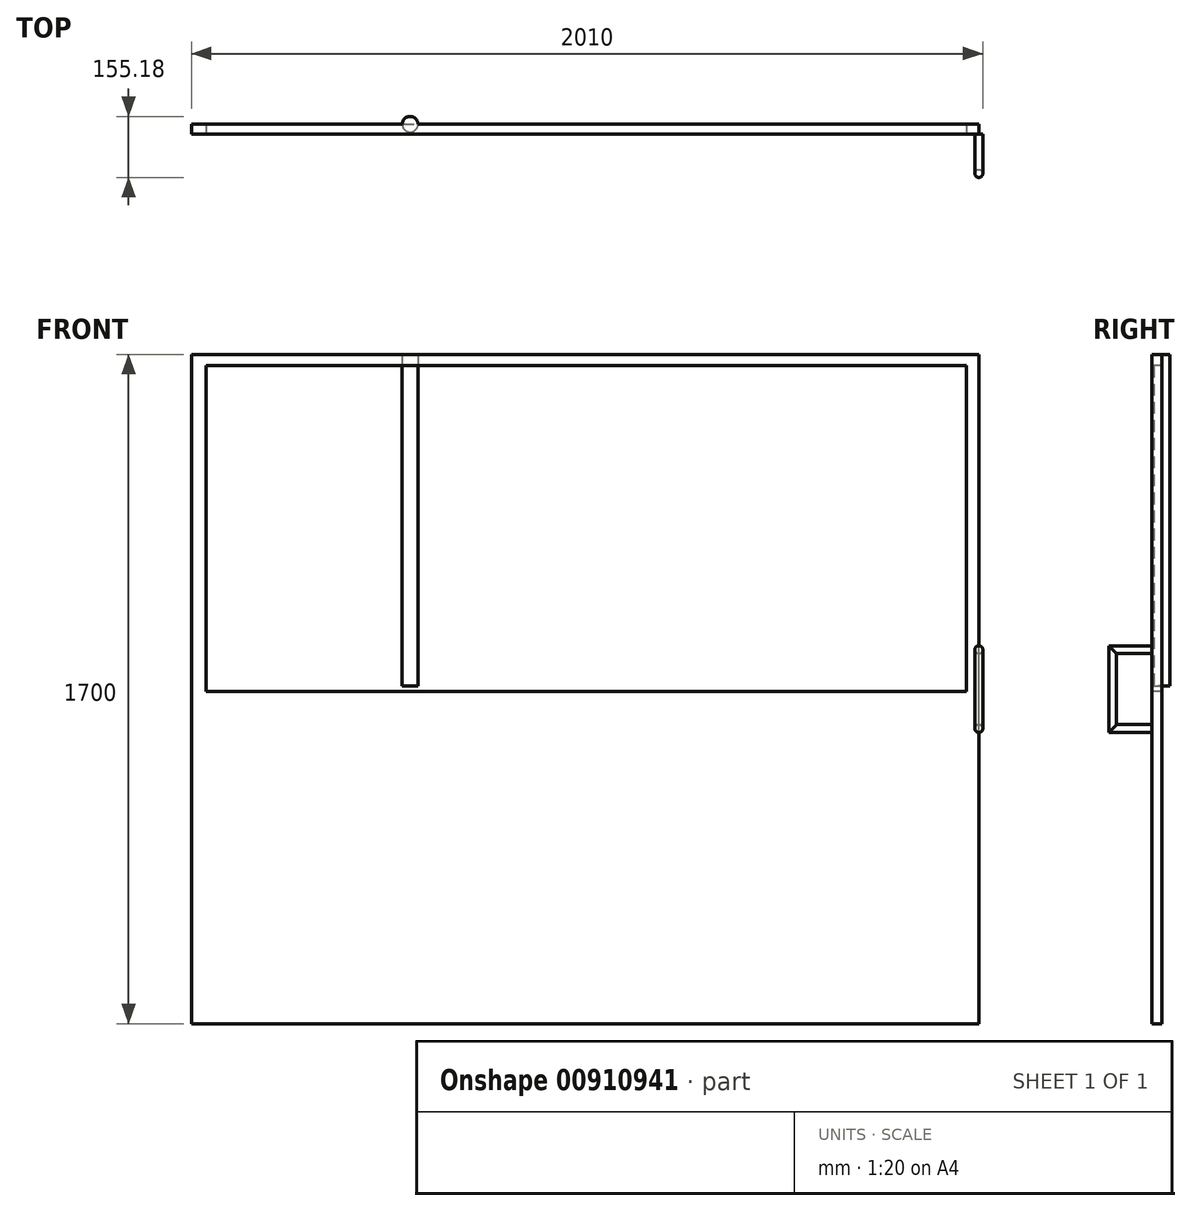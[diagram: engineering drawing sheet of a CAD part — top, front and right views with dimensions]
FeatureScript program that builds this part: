
annotation { "Feature Type Name" : "Feature", "Feature Type Description" : "" }
export const myFeature = defineFeature(function(context is Context, id is Id, definition is map)
    precondition{}
    {
        {
            var Q0;
            Q0=qCreatedBy(makeId("Front.planeOp"),FACE);
            var sketch = newSketch(context, id + "F0", { "sketchPlane" : qUnion([Q0])});
            skLineSegment(sketch, "E0.bottom", {"start": v(0, 0) * mm, "end": v(1000, 0) * mm});
            skLineSegment(sketch, "E0.top", {"start": v(0, 1700) * mm, "end": v(1000, 1700) * mm});
            skLineSegment(sketch, "E0.right", {"start": v(1000, 0) * mm, "end": v(1000, 1700) * mm});
            skLineSegment(sketch, "E1.MirrorCS", {"start": v(0, 1700) * mm, "end": v(-1000, 1700) * mm});
            skLineSegment(sketch, "E2.MirrorCS", {"start": v(-1000, 0) * mm, "end": v(-1000, 1700) * mm});
            skLineSegment(sketch, "E3.MirrorCS", {"start": v(0, 0) * mm, "end": v(-1000, 0) * mm});
            skSolve(sketch);
        }
        {
            var Q0;
            Q0 = qSketchRegion(id + "F0", true);
            extrude(context, id + "F1", {"entities" : qUnion([Q0]), "depth" : 25 * mm, "offsetDistance" : 25 * mm});
        }
        {
            var Q0;
            Q0=makeQuery(id+"F1.opExtrude","SWEPT_FACE",FACE,{"disambiguationData":[OSD([sQuery(id+"F0.wireOp",EDGE,"E0.right")])]});
            var sketch = newSketch(context, id + "F2", { "sketchPlane" : qUnion([Q0])});
            skPoint(sketch, "E4.start.orphan", {"position": v(-25, 850) * mm});
            skLineSegment(sketch, "E5", {"start": v(-25, 950) * mm, "end": v(-125, 950) * mm});
            skLineSegment(sketch, "E6", {"start": v(-125, 950) * mm, "end": v(-125, 750) * mm});
            skLineSegment(sketch, "E7", {"start": v(-125, 750) * mm, "end": v(-25, 750) * mm});
            skSolve(sketch);
        }
        {
            var Q0;
            Q0=makeQuery(id+"F1.opExtrude","CAP_FACE",FACE,{"disambiguationData":[OSD([sQuery(id+"F0.wireOp",EDGE,"E0.bottom"),sQuery(id+"F0.wireOp",EDGE,"E0.top"),sQuery(id+"F0.wireOp",EDGE,"E0.right"),sQuery(id+"F0.wireOp",EDGE,"E1.MirrorCS"),sQuery(id+"F0.wireOp",EDGE,"E2.MirrorCS"),sQuery(id+"F0.wireOp",EDGE,"E3.MirrorCS")])],"isStart":false});
            var sketch = newSketch(context, id + "F3", { "sketchPlane" : qUnion([Q0])});
            skCircle(sketch, "E8", {"center": v(1000, 950.18) * mm, "radius": 10 * mm});
            skSolve(sketch);
        }
        {
            var Q0;
            {var subQ0=sQuery(id+"F3.wireOp",EDGE,"E8");var subQ1=makeQuery(id+"F1.opExtrude","CAP_EDGE",EDGE,{"disambiguationData":[OSD([sQuery(id+"F0.wireOp",EDGE,"E0.right")])],"isStart":false});var subQ2=makeQuery(id+"F3.imprint","INTERSECT",VERTEX,{"disambiguationData":[OD(0.0)],"derivedFrom":[subQ1,subQ0]});Q0=makeQuery(id+"F3.imprint","IMPRINT",FACE,{"disambiguationData":[TD([[makeQuery(id+"F3.imprint","IMPRINT",EDGE,{"disambiguationData":[TD([[subQ2,-1.0]])],"derivedFrom":subQ0}),1.0]])]});}
            var Q1;
            {var subQ0=sQuery(id+"F3.wireOp",EDGE,"E8");var subQ1=makeQuery(id+"F1.opExtrude","CAP_EDGE",EDGE,{"disambiguationData":[OSD([sQuery(id+"F0.wireOp",EDGE,"E0.right")])],"isStart":false});var subQ2=makeQuery(id+"F3.imprint","INTERSECT",VERTEX,{"disambiguationData":[OD(0.0)],"derivedFrom":[subQ1,subQ0]});Q1=makeQuery(id+"F3.imprint","IMPRINT",FACE,{"disambiguationData":[TD([[makeQuery(id+"F3.imprint","IMPRINT",EDGE,{"disambiguationData":[TD([[subQ2,1.0]])],"derivedFrom":subQ0}),1.0]])]});}
            var Q2;
            Q2=sQuery(id+"F2.wireOp",EDGE,"E5");
            var Q3;
            Q3=sQuery(id+"F2.wireOp",EDGE,"E6");
            var Q4;
            Q4=sQuery(id+"F2.wireOp",EDGE,"E7");
            sweep(context, id + "F4", {"operationType" : NewBodyOperationType.ADD, "profiles" : qUnion([Q0, Q1]), "path" : qUnion([Q2, Q3, Q4])});
        }
        {
            var Q0;
            Q0=makeQuery(id+"F1.opExtrude","CAP_FACE",FACE,{"disambiguationData":[OSD([sQuery(id+"F0.wireOp",EDGE,"E0.bottom"),sQuery(id+"F0.wireOp",EDGE,"E0.top"),sQuery(id+"F0.wireOp",EDGE,"E0.right"),sQuery(id+"F0.wireOp",EDGE,"E1.MirrorCS"),sQuery(id+"F0.wireOp",EDGE,"E2.MirrorCS"),sQuery(id+"F0.wireOp",EDGE,"E3.MirrorCS")])],"isStart":false});
            var sketch = newSketch(context, id + "F5", { "sketchPlane" : qUnion([Q0])});
            skLineSegment(sketch, "E9.bottom", {"start": v(-963.47, 1671.56) * mm, "end": v(968.33, 1671.56) * mm});
            skLineSegment(sketch, "E9.top", {"start": v(-963.47, 843.75) * mm, "end": v(968.33, 843.75) * mm});
            skLineSegment(sketch, "E9.left", {"start": v(-963.47, 1671.56) * mm, "end": v(-963.47, 843.75) * mm});
            skLineSegment(sketch, "E9.right", {"start": v(968.33, 1671.56) * mm, "end": v(968.33, 843.75) * mm});
            skSolve(sketch);
        }
        {
            var Q0;
            Q0=makeQuery(id+"F5.imprint","IMPRINT",FACE,{"disambiguationData":[TD([[makeQuery(id+"F5.imprint","IMPRINT",EDGE,{"derivedFrom":sQuery(id+"F5.wireOp",EDGE,"E9.bottom")}),-1.0]])]});
            extrude(context, id + "F6", {"entities" : qUnion([Q0]), "operationType" : NewBodyOperationType.REMOVE, "oppositeDirection" : true, "depth" : 25 * mm, "offsetDistance" : 25 * mm});
        }
        {
            var Q0;
            Q0=makeQuery(id+"F0.imprint","IMPRINT",FACE,{"disambiguationData":[TD([[makeQuery(id+"F0.imprint","IMPRINT",EDGE,{"derivedFrom":sQuery(id+"F0.wireOp",EDGE,"E0.bottom")}),1.0]])]});
            var sketch = newSketch(context, id + "F7", { "sketchPlane" : qUnion([Q0])});
            skLineSegment(sketch, "E10", {"start": v(-442.5, 1672.3) * mm, "end": v(-442.5, 844.34) * mm});
            skLineSegment(sketch, "E11", {"start": v(439.1, 1675.66) * mm, "end": v(439.1, 851.05) * mm});
            skPoint(sketch, "E12.start.orphan", {"position": v(0, 1689.07) * mm});
            skLineSegment(sketch, "E13", {"start": v(0, 847.7) * mm, "end": v(0, 1689.07) * mm});
            skCircle(sketch, "E14", {"center": v(-442.5, 844.34) * mm, "radius": 15 * mm});
            skCircle(sketch, "E15", {"center": v(0, 847.7) * mm, "radius": 15 * mm});
            skCircle(sketch, "E16", {"center": v(439.1, 851.05) * mm, "radius": 15 * mm});
            skSolve(sketch);
        }
        {
            var Q0;
            Q0=makeQuery(id+"F1.opExtrude","SWEPT_FACE",FACE,{"disambiguationData":[OSD([sQuery(id+"F0.wireOp",EDGE,"E0.top"),sQuery(id+"F0.wireOp",EDGE,"E1.MirrorCS")])]});
            var sketch = newSketch(context, id + "F8", { "sketchPlane" : qUnion([Q0])});
            skCircle(sketch, "E17", {"center": v(-444.8, 0) * mm, "radius": 20 * mm});
            skSolve(sketch);
        }
        {
            var Q0;
            {var subQ0=sQuery(id+"F8.wireOp",EDGE,"E17");var subQ1=makeQuery(id+"F1.opExtrude","CAP_EDGE",EDGE,{"disambiguationData":[OSD([sQuery(id+"F0.wireOp",EDGE,"E0.top"),sQuery(id+"F0.wireOp",EDGE,"E1.MirrorCS")])],"isStart":true});var subQ2=makeQuery(id+"F8.imprint","INTERSECT",VERTEX,{"disambiguationData":[OD(0.0)],"derivedFrom":[subQ1,subQ0]});Q0=makeQuery(id+"F8.imprint","IMPRINT",FACE,{"disambiguationData":[TD([[makeQuery(id+"F8.imprint","IMPRINT",EDGE,{"disambiguationData":[TD([[subQ2,1.0]])],"derivedFrom":subQ0}),1.0]])]});}
            var Q1;
            {var subQ0=sQuery(id+"F8.wireOp",EDGE,"E17");var subQ1=makeQuery(id+"F1.opExtrude","CAP_EDGE",EDGE,{"disambiguationData":[OSD([sQuery(id+"F0.wireOp",EDGE,"E0.top"),sQuery(id+"F0.wireOp",EDGE,"E1.MirrorCS")])],"isStart":true});var subQ2=makeQuery(id+"F8.imprint","INTERSECT",VERTEX,{"disambiguationData":[OD(0.0)],"derivedFrom":[subQ1,subQ0]});Q1=makeQuery(id+"F8.imprint","IMPRINT",FACE,{"disambiguationData":[TD([[makeQuery(id+"F8.imprint","IMPRINT",EDGE,{"disambiguationData":[TD([[subQ2,-1.0]])],"derivedFrom":subQ0}),1.0]])]});}
            var Q2;
            Q2=sQuery(id+"F7.wireOp",EDGE,"E13");
            sweep(context, id + "F9", {"operationType" : NewBodyOperationType.ADD, "profiles" : qUnion([Q0, Q1]), "path" : qUnion([Q2])});
        }
    });
